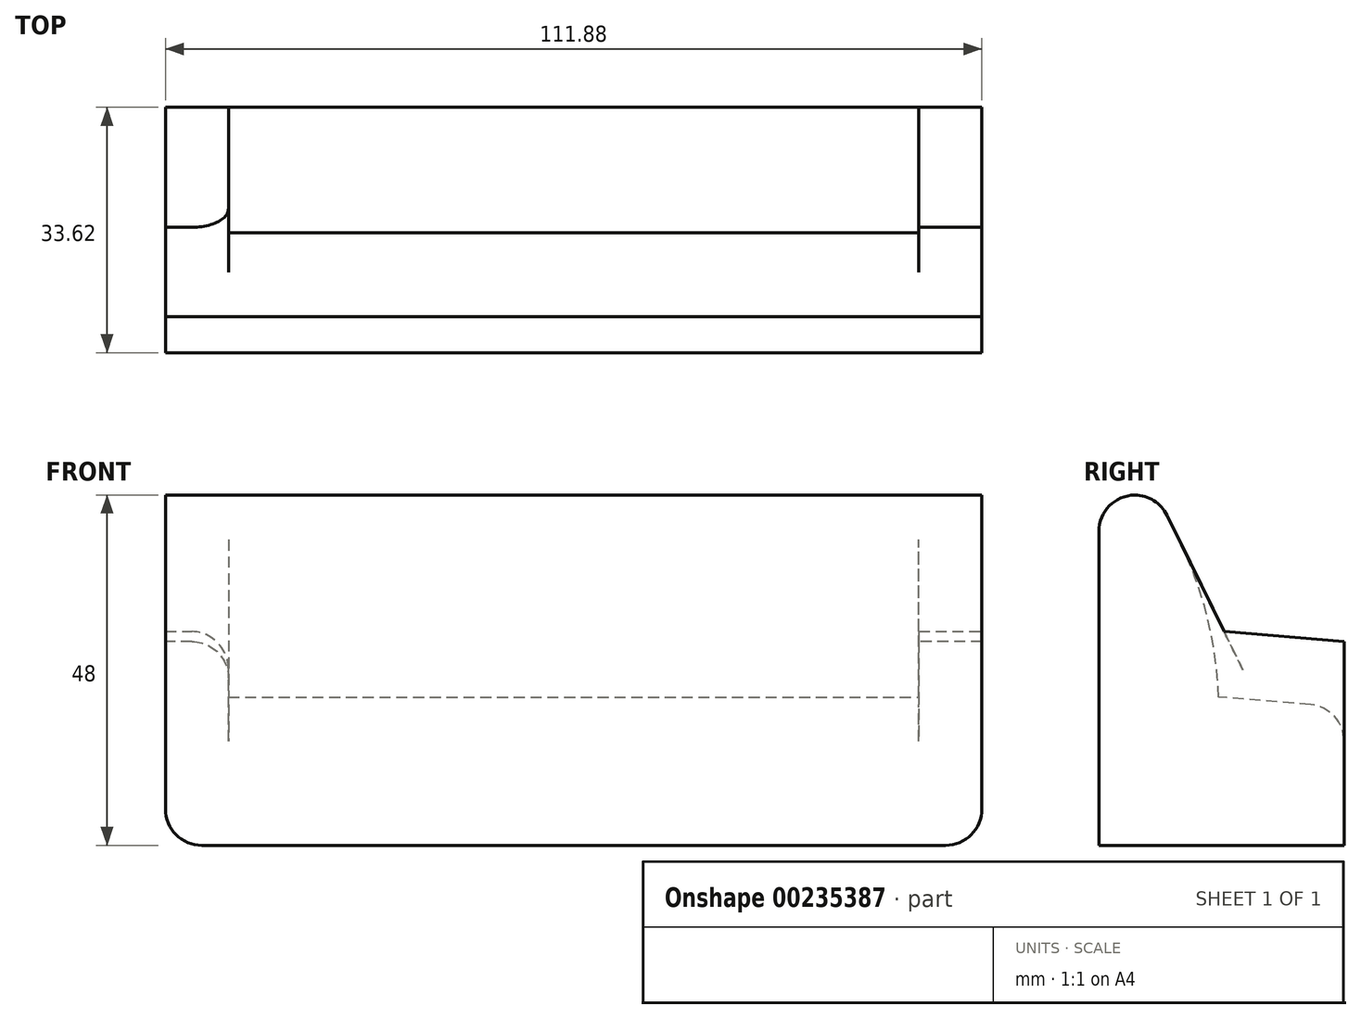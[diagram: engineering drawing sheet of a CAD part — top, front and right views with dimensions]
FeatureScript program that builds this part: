
annotation { "Feature Type Name" : "Feature", "Feature Type Description" : "" }
export const myFeature = defineFeature(function(context is Context, id is Id, definition is map)
    precondition{}
    {
        {
            var Q0;
            Q0=qCreatedBy(makeId("Top.planeOp"),FACE);
            var sketch = newSketch(context, id + "F0", { "sketchPlane" : qUnion([Q0])});
            skLineSegment(sketch, "E0", {"start": v(-63.02, -11.28) * mm, "end": v(48.86, -11.28) * mm});
            skLineSegment(sketch, "E1", {"start": v(48.86, -11.28) * mm, "end": v(48.86, -44.9) * mm});
            skLineSegment(sketch, "E2", {"start": v(48.86, -44.9) * mm, "end": v(-63.02, -44.9) * mm});
            skLineSegment(sketch, "E3", {"start": v(-63.02, -11.28) * mm, "end": v(-63.02, -44.9) * mm});
            skSolve(sketch);
        }
        {
            var Q0;
            Q0=makeQuery(id+"F0.imprint","IMPRINT",FACE,{"disambiguationData":[TD([[makeQuery(id+"F0.imprint","IMPRINT",EDGE,{"derivedFrom":sQuery(id+"F0.wireOp",EDGE,"E0")}),-1.0]])]});
            extrude(context, id + "F1", {"entities" : qUnion([Q0]), "depth" : 48 * mm});
        }
        {
            var Q0;
            Q0=qCreatedBy(makeId("Right.planeOp"),FACE);
            var sketch = newSketch(context, id + "F2", { "sketchPlane" : qUnion([Q0])});
            skLineSegment(sketch, "E4", {"start": v(-39.98, 54.26) * mm, "end": v(-27.73, 29.3) * mm});
            skLineSegment(sketch, "E5", {"start": v(-27.73, 29.3) * mm, "end": v(-4.68, 27.37) * mm});
            skLineSegment(sketch, "E6", {"start": v(-4.68, 27.37) * mm, "end": v(-2.27, 56.28) * mm});
            skLineSegment(sketch, "E7", {"start": v(-2.27, 56.28) * mm, "end": v(-39.98, 54.26) * mm});
            skSolve(sketch);
        }
        {
            var Q0;
            Q0=makeQuery(id+"F2.imprint","IMPRINT",FACE,{"disambiguationData":[TD([[makeQuery(id+"F2.imprint","IMPRINT",EDGE,{"derivedFrom":sQuery(id+"F2.wireOp",EDGE,"E4")}),1.0]])]});
            extrude(context, id + "F3", {"entities" : qUnion([Q0]), "operationType" : NewBodyOperationType.REMOVE, "endBound" : BoundingType.SYMMETRIC, "oppositeDirection" : true, "depth" : 184 * mm});
        }
        {
            var Q0;
            Q0=makeQuery(id+"F3.boolean.opBoolean","COPY",FACE,{"derivedFrom":makeQuery(id+"F3.opExtrude","SWEPT_FACE",FACE,{"disambiguationData":[OSD([sQuery(id+"F2.wireOp",EDGE,"E5")])]})});
            var sketch = newSketch(context, id + "F4", { "sketchPlane" : qUnion([Q0])});
            skLineSegment(sketch, "E8", {"start": v(-54.38, -8.75) * mm, "end": v(-54.38, -30.07) * mm});
            skLineSegment(sketch, "E9", {"start": v(-54.38, -30.07) * mm, "end": v(40.22, -30.07) * mm});
            skLineSegment(sketch, "E10", {"start": v(40.22, -30.07) * mm, "end": v(40.22, -5.85) * mm});
            skLineSegment(sketch, "E11", {"start": v(40.22, -5.85) * mm, "end": v(-54.38, -8.75) * mm});
            skSolve(sketch);
        }
        {
            var Q0;
            Q0 = qSketchRegion(id + "F4", true);
            extrude(context, id + "F5", {"entities" : qUnion([Q0]), "operationType" : NewBodyOperationType.REMOVE, "oppositeDirection" : true, "depth" : 9 * mm});
        }
        {
            var Q0;
            Q0=makeQuery(id+"F5.boolean.opBoolean","MERGE",EDGE,{"derivedFrom":[makeQuery(id+"F3.boolean.opBoolean","COPY",EDGE,{"derivedFrom":makeQuery(id+"F3.opExtrude","SWEPT_EDGE",EDGE,{"disambiguationData":[OSD([sQuery(id+"F2.wireOp",EDGE,"E4"),sQuery(id+"F2.wireOp",EDGE,"E5")])]})}),makeQuery(id+"F5.opExtrude","CAP_EDGE",EDGE,{"disambiguationData":[OSD([sQuery(id+"F4.wireOp",EDGE,"E9")])],"isStart":true})]});
            fillet(context, id + "F6", {"entities" : qUnion([Q0]), "radius" : 53.4 * mm, "tangentPropagation" : true, "allowEdgeOverflow" : false});
        }
        {
            var Q0;
            Q0=makeQuery(id+"F5.boolean.opBoolean","COPY",EDGE,{"derivedFrom":makeQuery(id+"F5.opExtrude","CAP_EDGE",EDGE,{"disambiguationData":[OSD([sQuery(id+"F4.wireOp",EDGE,"E8")])],"isStart":true})});
            var Q1;
            Q1=makeQuery(id+"F5.boolean.opBoolean","COPY",EDGE,{"derivedFrom":makeQuery(id+"F5.opExtrude","CAP_EDGE",EDGE,{"disambiguationData":[OSD([sQuery(id+"F4.wireOp",EDGE,"E10")])],"isStart":true})});
            fillet(context, id + "F7", {"entities" : qUnion([Q0, Q1]), "radius" : 5 * mm, "tangentPropagation" : true, "allowEdgeOverflow" : false});
        }
        {
            var Q0;
            Q0=makeQuery(id+"F5.boolean.opBoolean","INTERSECT",EDGE,{"derivedFrom":[makeQuery(id+"F1.opExtrude","SWEPT_FACE",FACE,{"disambiguationData":[OSD([sQuery(id+"F0.wireOp",EDGE,"E0")])]}),makeQuery(id+"F5.opExtrude","CAP_FACE",FACE,{"disambiguationData":[OSD([sQuery(id+"F4.wireOp",EDGE,"E8"),sQuery(id+"F4.wireOp",EDGE,"E9"),sQuery(id+"F4.wireOp",EDGE,"E10"),sQuery(id+"F4.wireOp",EDGE,"E11")])],"isStart":false})]});
            fillet(context, id + "F8", {"entities" : qUnion([Q0]), "radius" : 5 * mm, "tangentPropagation" : true, "allowEdgeOverflow" : false});
        }
        {
            var Q0;
            Q0=makeQuery(id+"F1.opExtrude","CAP_EDGE",EDGE,{"disambiguationData":[OSD([sQuery(id+"F0.wireOp",EDGE,"E3")])],"isStart":true});
            var Q1;
            Q1=makeQuery(id+"F1.opExtrude","CAP_EDGE",EDGE,{"disambiguationData":[OSD([sQuery(id+"F0.wireOp",EDGE,"E1")])],"isStart":true});
            fillet(context, id + "F9", {"entities" : qUnion([Q0, Q1]), "radius" : 5 * mm, "tangentPropagation" : true, "allowEdgeOverflow" : false});
        }
        {
            var Q0;
            Q0=makeQuery(id+"F1.opExtrude","CAP_EDGE",EDGE,{"disambiguationData":[OSD([sQuery(id+"F0.wireOp",EDGE,"E2")])],"isStart":false});
            var Q1;
            Q1=makeQuery(id+"F3.boolean.opBoolean","INTERSECT",EDGE,{"derivedFrom":[makeQuery(id+"F1.opExtrude","CAP_FACE",FACE,{"disambiguationData":[OSD([sQuery(id+"F0.wireOp",EDGE,"E0"),sQuery(id+"F0.wireOp",EDGE,"E1"),sQuery(id+"F0.wireOp",EDGE,"E2"),sQuery(id+"F0.wireOp",EDGE,"E3")])],"isStart":false}),makeQuery(id+"F3.opExtrude","SWEPT_FACE",FACE,{"disambiguationData":[OSD([sQuery(id+"F2.wireOp",EDGE,"E4")])]})]});
            fillet(context, id + "F10", {"entities" : qUnion([Q0, Q1]), "radius" : 5 * mm, "tangentPropagation" : true, "allowEdgeOverflow" : false});
        }
    });
